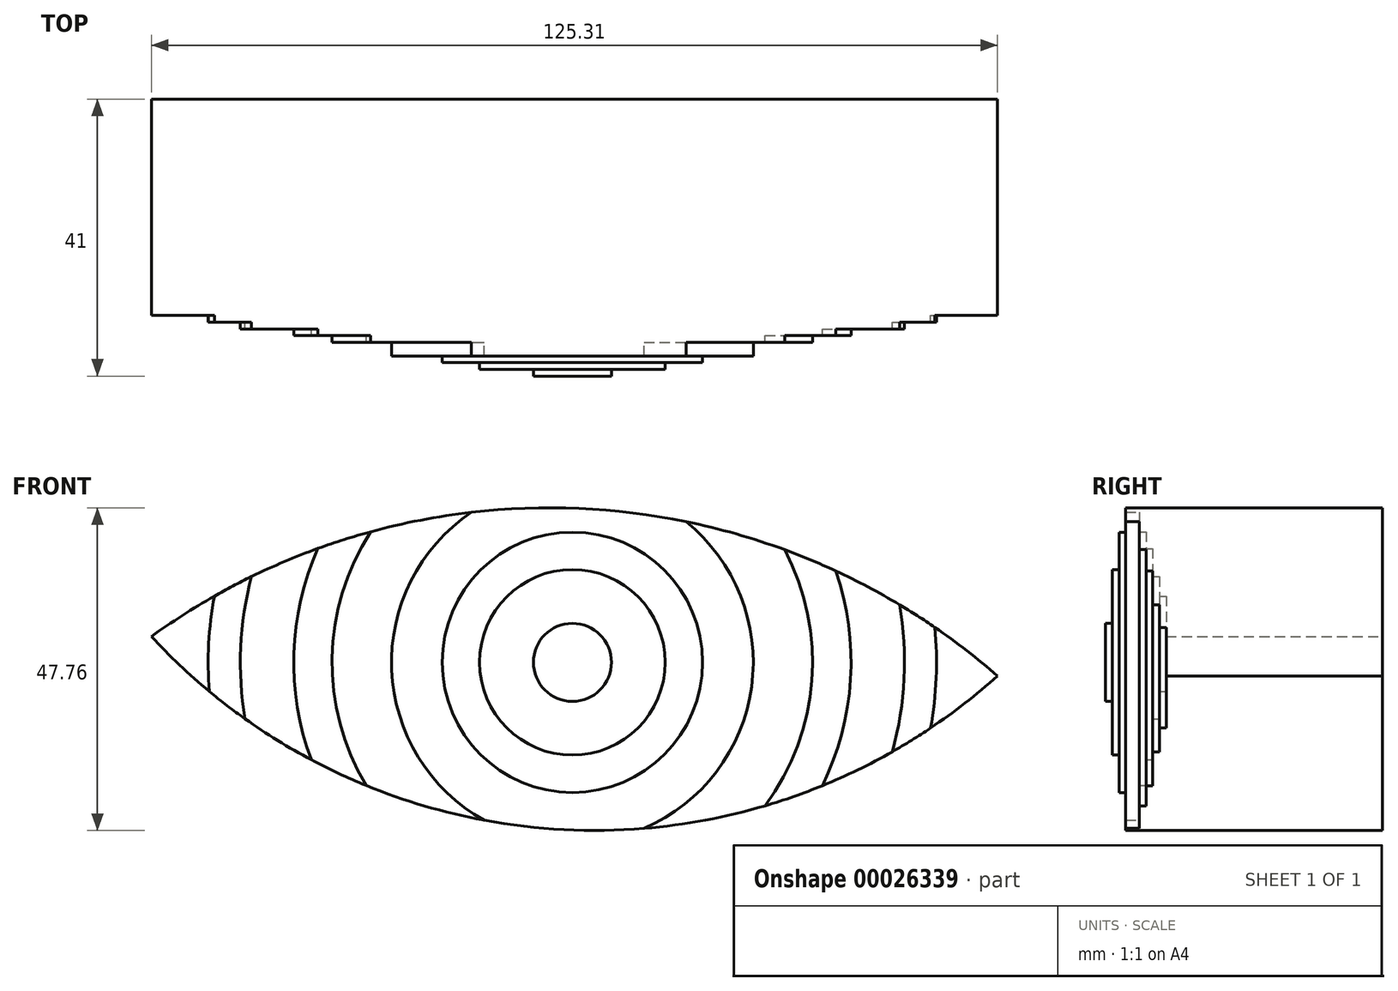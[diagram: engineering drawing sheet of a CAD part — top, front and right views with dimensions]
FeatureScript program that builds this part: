
annotation { "Feature Type Name" : "Feature", "Feature Type Description" : "" }
export const myFeature = defineFeature(function(context is Context, id is Id, definition is map)
    precondition{}
    {
        {
            var Q0;
            Q0=qCreatedBy(makeId("Front.planeOp"),FACE);
            var sketch = newSketch(context, id + "F0", { "sketchPlane" : qUnion([Q0])});
            skArc(sketch, "E0", {"start": v(61.14, 2.12) * mm, "mid": v(-0.5, 26.9) * mm, "end": v(-64.17, 7.97) * mm});
            skArc(sketch, "E1", {"start": v(-64.17, 7.97) * mm, "mid": v(-2.71, -20.65) * mm, "end": v(61.14, 2.12) * mm});
            skCircle(sketch, "E2", {"center": v(-1.82, 4.14) * mm, "radius": 5.78 * mm});
            skCircle(sketch, "E3", {"center": v(-1.82, 4.14) * mm, "radius": 13.74 * mm});
            skCircle(sketch, "E4", {"center": v(-1.82, 4.14) * mm, "radius": 19.28 * mm});
            skArc(sketch, "E5", {"start": v(-16.8, 26.34) * mm, "mid": v(-28.58, 3.02) * mm, "end": v(-14.89, -19.24) * mm});
            skArc(sketch, "E6", {"start": v(-31.68, 23.47) * mm, "mid": v(-37.39, 4.78) * mm, "end": v(-32.36, -14.1) * mm});
            skArc(sketch, "E7", {"start": v(-39.5, 21) * mm, "mid": v(-43.07, 5.45) * mm, "end": v(-40.5, -10.3) * mm});
            skArc(sketch, "E8", {"start": v(-49.34, 16.84) * mm, "mid": v(-50.96, 6.35) * mm, "end": v(-50.29, -4.24) * mm});
            skArc(sketch, "E9", {"start": v(-54.85, 13.94) * mm, "mid": v(-55.68, 6.9) * mm, "end": v(-55.58, -0.18) * mm});
            skArc(sketch, "E10.trimOffspring", {"start": v(8.82, -20.45) * mm, "mid": v(24.72, 0.5) * mm, "end": v(15.03, 24.96) * mm});
            skArc(sketch, "E11.trimOffspring", {"start": v(26.73, -17.1) * mm, "mid": v(33.66, 1.44) * mm, "end": v(29.61, 20.81) * mm});
            skArc(sketch, "E12.trimOffspring", {"start": v(35.2, -14.13) * mm, "mid": v(39.38, 1.57) * mm, "end": v(37.18, 17.68) * mm});
            skArc(sketch, "E13.trimOffspring", {"start": v(51.23, -5.6) * mm, "mid": v(52.07, 1.84) * mm, "end": v(51.87, 9.31) * mm});
            skArc(sketch, "E14.trimOffspring", {"start": v(45.56, -9.1) * mm, "mid": v(47.32, 1.73) * mm, "end": v(46.63, 12.68) * mm});
            skSolve(sketch);
        }
        {
            var Q0;
            Q0=makeQuery(id+"F0.imprint","IMPRINT",FACE,{"disambiguationData":[TD([[makeQuery(id+"F0.imprint","IMPRINT",EDGE,{"derivedFrom":sQuery(id+"F0.wireOp",EDGE,"E2")}),1.0]])]});
            extrude(context, id + "F1", {"entities" : qUnion([Q0]), "depth" : 41 * mm});
        }
        {
            var Q0;
            Q0=makeQuery(id+"F0.imprint","IMPRINT",FACE,{"disambiguationData":[TD([[makeQuery(id+"F0.imprint","IMPRINT",EDGE,{"derivedFrom":sQuery(id+"F0.wireOp",EDGE,"E2")}),-1.0]])]});
            extrude(context, id + "F2", {"entities" : qUnion([Q0]), "operationType" : NewBodyOperationType.ADD, "depth" : 40 * mm});
        }
        {
            var Q0;
            Q0=makeQuery(id+"F0.imprint","IMPRINT",FACE,{"disambiguationData":[TD([[makeQuery(id+"F0.imprint","IMPRINT",EDGE,{"derivedFrom":sQuery(id+"F0.wireOp",EDGE,"E3")}),-1.0]])]});
            extrude(context, id + "F3", {"entities" : qUnion([Q0]), "operationType" : NewBodyOperationType.ADD, "depth" : 39 * mm});
        }
        {
            var Q0;
            Q0=makeQuery(id+"F0.imprint","IMPRINT",FACE,{"disambiguationData":[TD([[makeQuery(id+"F0.imprint","IMPRINT",EDGE,{"derivedFrom":sQuery(id+"F0.wireOp",EDGE,"E4")}),-1.0]])]});
            extrude(context, id + "F4", {"entities" : qUnion([Q0]), "operationType" : NewBodyOperationType.ADD, "depth" : 38 * mm});
        }
        {
            var Q0;
            {var subQ1=sQuery(id+"F0.wireOp",EDGE,"E5");Q0=makeQuery(id+"F0.imprint","IMPRINT",FACE,{"disambiguationData":[TD([[makeQuery(id+"F0.imprint","IMPRINT",EDGE,{"derivedFrom":subQ1}),-1.0]])]});}
            var Q1;
            {var subQ1=sQuery(id+"F0.wireOp",EDGE,"E10.trimOffspring");Q1=makeQuery(id+"F0.imprint","IMPRINT",FACE,{"disambiguationData":[TD([[makeQuery(id+"F0.imprint","IMPRINT",EDGE,{"derivedFrom":subQ1}),-1.0]])]});}
            extrude(context, id + "F5", {"entities" : qUnion([Q0, Q1]), "operationType" : NewBodyOperationType.ADD, "depth" : 36 * mm});
        }
        {
            var Q0;
            {var subQ1=sQuery(id+"F0.wireOp",EDGE,"E6");Q0=makeQuery(id+"F0.imprint","IMPRINT",FACE,{"disambiguationData":[TD([[makeQuery(id+"F0.imprint","IMPRINT",EDGE,{"derivedFrom":subQ1}),-1.0]])]});}
            var Q1;
            {var subQ1=sQuery(id+"F0.wireOp",EDGE,"E11.trimOffspring");Q1=makeQuery(id+"F0.imprint","IMPRINT",FACE,{"disambiguationData":[TD([[makeQuery(id+"F0.imprint","IMPRINT",EDGE,{"derivedFrom":subQ1}),-1.0]])]});}
            extrude(context, id + "F6", {"entities" : qUnion([Q0, Q1]), "operationType" : NewBodyOperationType.ADD, "depth" : 35 * mm});
        }
        {
            var Q0;
            {var subQ1=sQuery(id+"F0.wireOp",EDGE,"E7");Q0=makeQuery(id+"F0.imprint","IMPRINT",FACE,{"disambiguationData":[TD([[makeQuery(id+"F0.imprint","IMPRINT",EDGE,{"derivedFrom":subQ1}),-1.0]])]});}
            var Q1;
            {var subQ1=sQuery(id+"F0.wireOp",EDGE,"E12.trimOffspring");Q1=makeQuery(id+"F0.imprint","IMPRINT",FACE,{"disambiguationData":[TD([[makeQuery(id+"F0.imprint","IMPRINT",EDGE,{"derivedFrom":subQ1}),-1.0]])]});}
            extrude(context, id + "F7", {"entities" : qUnion([Q0, Q1]), "operationType" : NewBodyOperationType.ADD, "depth" : 34 * mm});
        }
        {
            var Q0;
            {var subQ1=sQuery(id+"F0.wireOp",EDGE,"E8");Q0=makeQuery(id+"F0.imprint","IMPRINT",FACE,{"disambiguationData":[TD([[makeQuery(id+"F0.imprint","IMPRINT",EDGE,{"derivedFrom":subQ1}),-1.0]])]});}
            var Q1;
            {var subQ1=sQuery(id+"F0.wireOp",EDGE,"E13.trimOffspring");Q1=makeQuery(id+"F0.imprint","IMPRINT",FACE,{"disambiguationData":[TD([[makeQuery(id+"F0.imprint","IMPRINT",EDGE,{"derivedFrom":subQ1}),1.0]])]});}
            extrude(context, id + "F8", {"entities" : qUnion([Q0, Q1]), "operationType" : NewBodyOperationType.ADD, "depth" : 33 * mm});
        }
        {
            var Q0;
            {var subQ0=sQuery(id+"F0.wireOp",EDGE,"E9");Q0=makeQuery(id+"F0.imprint","IMPRINT",FACE,{"disambiguationData":[TD([[makeQuery(id+"F0.imprint","IMPRINT",EDGE,{"derivedFrom":subQ0}),-1.0]])]});}
            var Q1;
            {var subQ0=sQuery(id+"F0.wireOp",EDGE,"E13.trimOffspring");Q1=makeQuery(id+"F0.imprint","IMPRINT",FACE,{"disambiguationData":[TD([[makeQuery(id+"F0.imprint","IMPRINT",EDGE,{"derivedFrom":subQ0}),-1.0]])]});}
            extrude(context, id + "F9", {"entities" : qUnion([Q0, Q1]), "operationType" : NewBodyOperationType.ADD, "depth" : 32 * mm});
        }
    });
